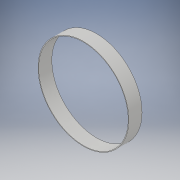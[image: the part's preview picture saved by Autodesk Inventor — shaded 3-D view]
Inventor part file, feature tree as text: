
AUTODESK INVENTOR PART (.ipt)
format: ipt  version: 2019 (Build 230136000, 136)  size: 104,448 bytes
history: native  units: mm
features: extrude x2, sketch x2
ambient origin geometry x8: Origin, YZ Plane, XZ Plane, XY Plane, X Axis, Y Axis, Z Axis, Center Point
bodies: Solid1 (feature_tree)
feature tree (4):
  extrude  "Extrusion1"  Depth=9.45mm TaperAngle=0.0deg
  extrude  "Extrusion2"  Depth=9.45mm TaperAngle=0.0deg
  sketch  "Sketch1"  dims[d0=65.38mm d1=9.45mm d2=0.0mm]
  sketch  "Sketch2"  dims[d3=64.4mm d4=9.45mm d5=0.0mm]
